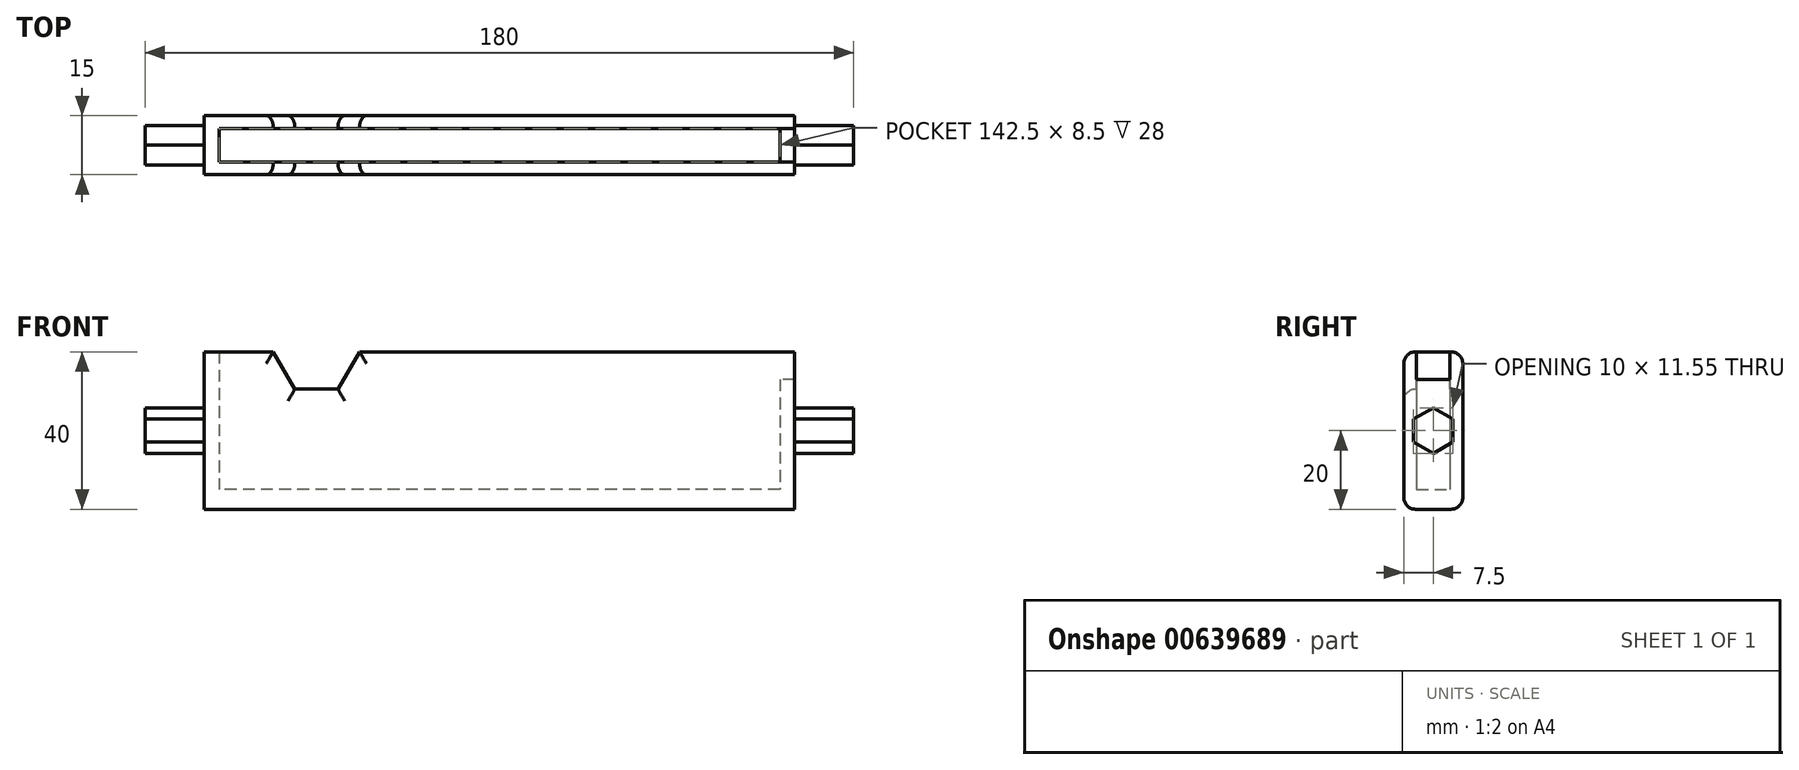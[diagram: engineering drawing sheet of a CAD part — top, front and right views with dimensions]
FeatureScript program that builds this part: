
annotation { "Feature Type Name" : "Feature", "Feature Type Description" : "" }
export const myFeature = defineFeature(function(context is Context, id is Id, definition is map)
    precondition{}
    {
        {
            var Q0;
            Q0=qCreatedBy(makeId("Front.planeOp"),FACE);
            var sketch = newSketch(context, id + "F0", { "sketchPlane" : qUnion([Q0])});
            skLineSegment(sketch, "E0.bottom", {"start": v(75, 20) * mm, "end": v(-75, 20) * mm});
            skLineSegment(sketch, "E0.top", {"start": v(75, -20) * mm, "end": v(-75, -20) * mm});
            skLineSegment(sketch, "E0.left", {"start": v(75, 20) * mm, "end": v(75, -20) * mm});
            skLineSegment(sketch, "E0.right", {"start": v(-75, 20) * mm, "end": v(-75, -20) * mm});
            skPoint(sketch, "E0.middle", {"position": v(0, 0) * mm});
            skCircle(sketch, "E1.cCircle", {"center": v(-46.5, 20) * mm, "radius": 9.5 * mm, "construction": true});
            skLineSegment(sketch, "E1.2", {"start": v(-35.53, 20) * mm, "end": v(-41.02, 10.5) * mm});
            skLineSegment(sketch, "E1.3", {"start": v(-41.02, 10.5) * mm, "end": v(-51.98, 10.5) * mm});
            skLineSegment(sketch, "E1.4", {"start": v(-51.98, 10.5) * mm, "end": v(-57.47, 20) * mm});
            skPoint(sketch, "E1.0.midPoint", {"position": v(-46.5, 29.5) * mm});
            skLineSegment(sketch, "E2", {"start": v(-75, 20) * mm, "end": v(-46.5, 20) * mm});
            skSolve(sketch);
        }
        {
            var Q0;
            Q0=makeQuery(id+"F0.imprint","IMPRINT",FACE,{"disambiguationData":[TD([[makeQuery(id+"F0.imprint","IMPRINT",EDGE,{"derivedFrom":sQuery(id+"F0.wireOp",EDGE,"E0.top")}),-1.0]])]});
            extrude(context, id + "F1", {"entities" : qUnion([Q0]), "endBound" : BoundingType.SYMMETRIC, "depth" : 15 * mm, "offsetDistance" : 25 * mm, "hasSecondDirection" : true, "secondDirectionOppositeDirection" : true, "secondDirectionDepth" : 25 * mm});
        }
        {
            var Q0;
            Q0=qCreatedBy(makeId("Front.planeOp"),FACE);
            var sketch = newSketch(context, id + "F2", { "sketchPlane" : qUnion([Q0])});
            skLineSegment(sketch, "E3.bottom", {"start": v(71.25, 55) * mm, "end": v(-71.25, 55) * mm});
            skLineSegment(sketch, "E3.top", {"start": v(71.25, -15) * mm, "end": v(-71.25, -15) * mm});
            skLineSegment(sketch, "E3.left", {"start": v(71.25, 55) * mm, "end": v(71.25, -15) * mm});
            skLineSegment(sketch, "E3.right", {"start": v(-71.25, 55) * mm, "end": v(-71.25, -15) * mm});
            skPoint(sketch, "E3.middle", {"position": v(0, 20) * mm});
            skLineSegment(sketch, "E4", {"start": v(71.25, 55) * mm, "end": v(81.25, 55) * mm});
            skLineSegment(sketch, "E5", {"start": v(81.25, 55) * mm, "end": v(81.25, 13) * mm});
            skLineSegment(sketch, "E6", {"start": v(81.25, 13) * mm, "end": v(71.25, 13) * mm});
            skPoint(sketch, "E6.endSnap0", {"position": v(71.25, 20) * mm});
            skSolve(sketch);
        }
        {
            var Q0;
            Q0 = qSketchRegion(id + "F2", true);
            extrude(context, id + "F3", {"entities" : qUnion([Q0]), "operationType" : NewBodyOperationType.REMOVE, "endBound" : BoundingType.SYMMETRIC, "depth" : 8.5 * mm, "offsetDistance" : 25 * mm});
        }
        {
            var Q0;
            Q0=qCreatedBy(makeId("Right.planeOp"),FACE);
            cPlane(context, id + "F4", {"entities" : qUnion([Q0]), "cplaneType" : CPlaneType.OFFSET, "offset" : 75 * mm, "width" : 150 * mm, "height" : 150 * mm});
        }
        {
            var Q0;
            Q0=qCreatedBy(id+"F4.planeOp",FACE);
            var sketch = newSketch(context, id + "F5", { "sketchPlane" : qUnion([Q0])});
            skCircle(sketch, "E7.cCircle", {"center": v(0, 0) * mm, "radius": 5 * mm, "construction": true});
            skLineSegment(sketch, "E7.0", {"start": v(5, 2.89) * mm, "end": v(5, -2.89) * mm});
            skLineSegment(sketch, "E7.1", {"start": v(5, -2.89) * mm, "end": v(0, -5.77) * mm});
            skLineSegment(sketch, "E7.2", {"start": v(0, -5.77) * mm, "end": v(-5, -2.89) * mm});
            skLineSegment(sketch, "E7.3", {"start": v(-5, -2.89) * mm, "end": v(-5, 2.89) * mm});
            skLineSegment(sketch, "E7.4", {"start": v(-5, 2.89) * mm, "end": v(0, 5.77) * mm});
            skLineSegment(sketch, "E7.5", {"start": v(0, 5.77) * mm, "end": v(5, 2.89) * mm});
            skPoint(sketch, "E7.0.midPoint", {"position": v(5, 0) * mm});
            skSolve(sketch);
        }
        {
            var Q0;
            Q0 = qSketchRegion(id + "F5", true);
            extrude(context, id + "F6", {"entities" : qUnion([Q0]), "depth" : 15 * mm, "offsetDistance" : 25 * mm});
        }
        {
            var Q0;
            Q0=makeQuery(id+"F6.opExtrude","SWEPT_BODY",BODY,{"disambiguationData":[OSD([sQuery(id+"F5.wireOp",EDGE,"E7.0"),sQuery(id+"F5.wireOp",EDGE,"E7.1"),sQuery(id+"F5.wireOp",EDGE,"E7.2"),sQuery(id+"F5.wireOp",EDGE,"E7.3"),sQuery(id+"F5.wireOp",EDGE,"E7.4"),sQuery(id+"F5.wireOp",EDGE,"E7.5")])]});
            var Q1;
            Q1=qCreatedBy(makeId("Right.planeOp"),FACE);
            mirror(context, id + "F7", {"operationType" : NewBodyOperationType.ADD, "entities" : qUnion([Q0]), "mirrorPlane" : qUnion([Q1])});
        }
        {
            var Q0;
            Q0=makeQuery(id+"F1.opExtrude","CAP_EDGE",EDGE,{"disambiguationData":[OSD([sQuery(id+"F0.wireOp",EDGE,"E0.top")])],"isStart":false});
            var Q1;
            Q1=makeQuery(id+"F1.opExtrude","CAP_EDGE",EDGE,{"disambiguationData":[OSD([sQuery(id+"F0.wireOp",EDGE,"E0.top")])],"isStart":true});
            var Q2;
            Q2=makeQuery(id+"F1.opExtrude","CAP_EDGE",EDGE,{"disambiguationData":[OSD([sQuery(id+"F0.wireOp",EDGE,"E0.bottom")])],"isStart":false});
            var Q3;
            Q3=makeQuery(id+"F1.opExtrude","CAP_EDGE",EDGE,{"disambiguationData":[OSD([sQuery(id+"F0.wireOp",EDGE,"E2")])],"isStart":false});
            var Q4;
            Q4=makeQuery(id+"F1.opExtrude","CAP_EDGE",EDGE,{"disambiguationData":[OSD([sQuery(id+"F0.wireOp",EDGE,"E2")])],"isStart":true});
            var Q5;
            Q5=makeQuery(id+"F1.opExtrude","CAP_EDGE",EDGE,{"disambiguationData":[OSD([sQuery(id+"F0.wireOp",EDGE,"E0.bottom")])],"isStart":true});
            var Q6;
            Q6=makeQuery(id+"F1.opExtrude","CAP_EDGE",EDGE,{"disambiguationData":[OSD([sQuery(id+"F0.wireOp",EDGE,"E1.4")])],"isStart":false});
            var Q7;
            Q7=makeQuery(id+"F1.opExtrude","CAP_EDGE",EDGE,{"disambiguationData":[OSD([sQuery(id+"F0.wireOp",EDGE,"E1.3")])],"isStart":false});
            var Q8;
            Q8=makeQuery(id+"F1.opExtrude","CAP_EDGE",EDGE,{"disambiguationData":[OSD([sQuery(id+"F0.wireOp",EDGE,"E1.2")])],"isStart":false});
            var Q9;
            Q9=makeQuery(id+"F1.opExtrude","CAP_EDGE",EDGE,{"disambiguationData":[OSD([sQuery(id+"F0.wireOp",EDGE,"E1.2")])],"isStart":true});
            var Q10;
            Q10=makeQuery(id+"F1.opExtrude","CAP_EDGE",EDGE,{"disambiguationData":[OSD([sQuery(id+"F0.wireOp",EDGE,"E1.3")])],"isStart":true});
            var Q11;
            Q11=makeQuery(id+"F1.opExtrude","CAP_EDGE",EDGE,{"disambiguationData":[OSD([sQuery(id+"F0.wireOp",EDGE,"E1.4")])],"isStart":true});
            fillet(context, id + "F8", {"entities" : qUnion([Q0, Q1, Q2, Q3, Q4, Q5, Q6, Q7, Q8, Q9, Q10, Q11]), "radius" : 3 * mm, "tangentPropagation" : true, "allowEdgeOverflow" : false});
        }
    });
